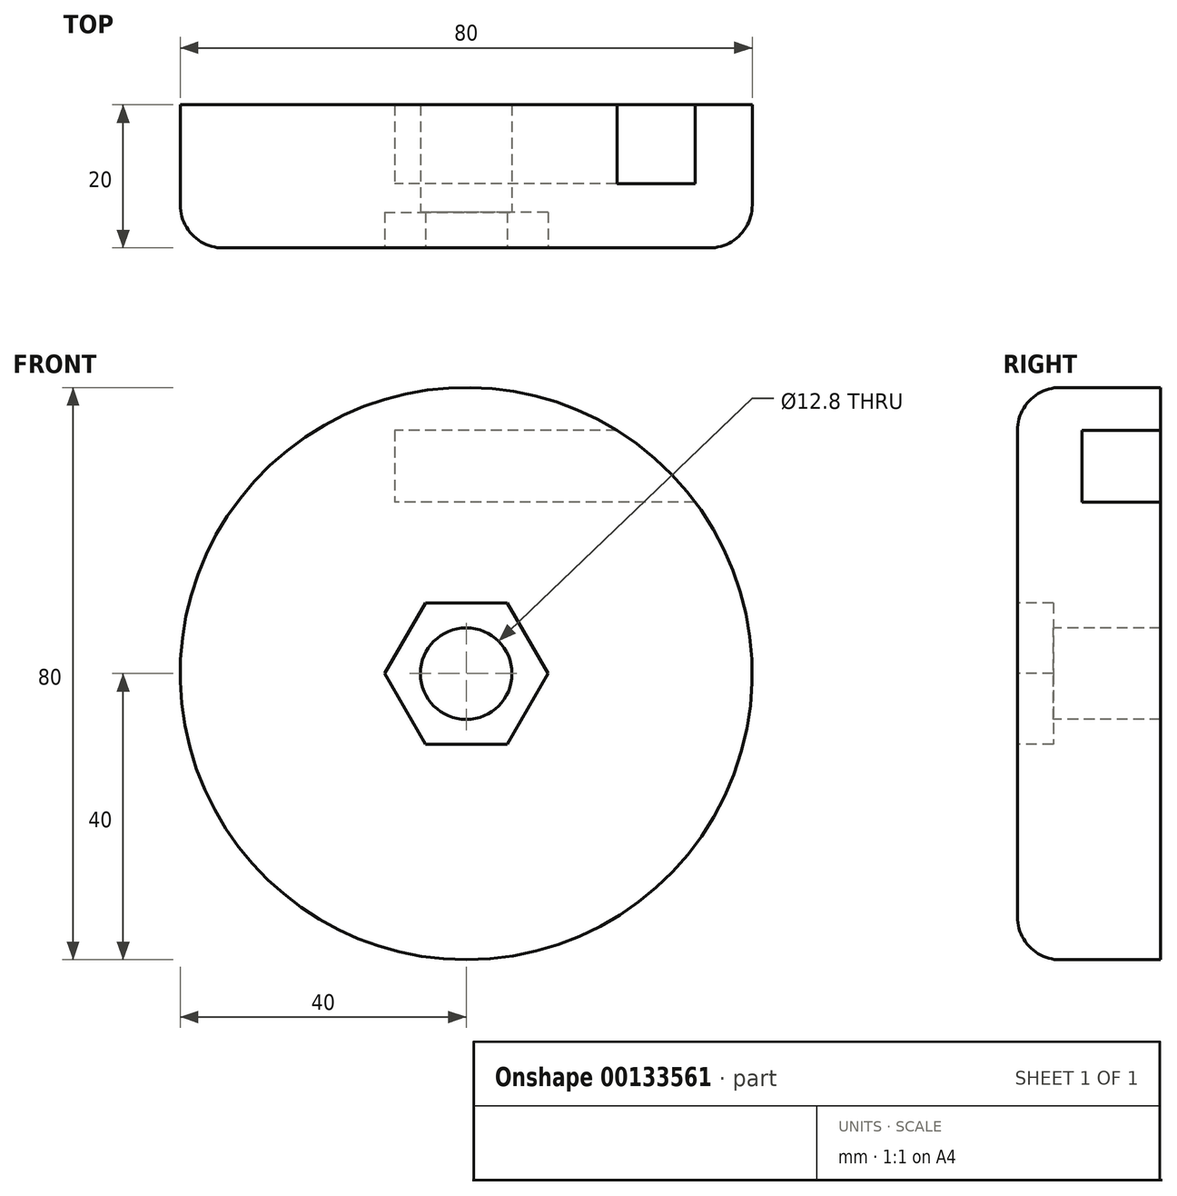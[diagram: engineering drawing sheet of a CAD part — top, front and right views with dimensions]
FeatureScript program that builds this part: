
annotation { "Feature Type Name" : "Feature", "Feature Type Description" : "" }
export const myFeature = defineFeature(function(context is Context, id is Id, definition is map)
    precondition{}
    {
        {
            var Q0;
            Q0=qCreatedBy(makeId("Front.planeOp"),FACE);
            var sketch = newSketch(context, id + "F0", { "sketchPlane" : qUnion([Q0])});
            skCircle(sketch, "E0", {"center": v(0, 0) * mm, "radius": 40 * mm});
            skSolve(sketch);
        }
        {
            var Q0;
            Q0 = qSketchRegion(id + "F0", true);
            extrude(context, id + "F1", {"entities" : qUnion([Q0]), "depth" : 20 * mm});
        }
        {
            var Q0;
            Q0=qCreatedBy(makeId("Right.planeOp"),FACE);
            var sketch = newSketch(context, id + "F2", { "sketchPlane" : qUnion([Q0])});
            skLineSegment(sketch, "E1.bottom", {"start": v(0, 34) * mm, "end": v(-11, 34) * mm});
            skLineSegment(sketch, "E1.top", {"start": v(0, 24) * mm, "end": v(-11, 24) * mm});
            skLineSegment(sketch, "E1.left", {"start": v(0, 34) * mm, "end": v(0, 24) * mm});
            skLineSegment(sketch, "E1.right", {"start": v(-11, 34) * mm, "end": v(-11, 24) * mm});
            skSolve(sketch);
        }
        {
            var Q0;
            Q0 = qSketchRegion(id + "F2", true);
            extrude(context, id + "F3", {"entities" : qUnion([Q0]), "operationType" : NewBodyOperationType.REMOVE, "depth" : 50 * mm, "hasSecondDirection" : true, "secondDirectionOppositeDirection" : true, "secondDirectionDepth" : 10 * mm});
        }
        {
            var Q0;
            Q0=makeQuery(id+"F1.opExtrude","CAP_EDGE",EDGE,{"disambiguationData":[OSD([sQuery(id+"F0.wireOp",EDGE,"E0")])],"isStart":false});
            fillet(context, id + "F4", {"entities" : qUnion([Q0]), "radius" : 6 * mm, "tangentPropagation" : true, "allowEdgeOverflow" : false});
        }
        {
            var Q0;
            Q0=makeQuery(id+"F1.opExtrude","CAP_FACE",FACE,{"disambiguationData":[OSD([sQuery(id+"F0.wireOp",EDGE,"E0")])],"isStart":false});
            var sketch = newSketch(context, id + "F5", { "sketchPlane" : qUnion([Q0])});
            skCircle(sketch, "E2.cCircle", {"center": v(0, 0) * mm, "radius": 9.9 * mm, "construction": true});
            skLineSegment(sketch, "E2.0", {"start": v(5.72, -9.9) * mm, "end": v(-5.72, -9.9) * mm});
            skLineSegment(sketch, "E2.1", {"start": v(-5.72, -9.9) * mm, "end": v(-11.43, 0) * mm});
            skLineSegment(sketch, "E2.2", {"start": v(-11.43, 0) * mm, "end": v(-5.72, 9.9) * mm});
            skLineSegment(sketch, "E2.3", {"start": v(-5.72, 9.9) * mm, "end": v(5.72, 9.9) * mm});
            skLineSegment(sketch, "E2.4", {"start": v(5.72, 9.9) * mm, "end": v(11.43, 0) * mm});
            skLineSegment(sketch, "E2.5", {"start": v(11.43, 0) * mm, "end": v(5.72, -9.9) * mm});
            skPoint(sketch, "E2.0.midPoint", {"position": v(0, -9.9) * mm});
            skSolve(sketch);
        }
        {
            var Q0;
            Q0 = qSketchRegion(id + "F5", true);
            extrude(context, id + "F6", {"entities" : qUnion([Q0]), "operationType" : NewBodyOperationType.REMOVE, "oppositeDirection" : true, "depth" : 5 * mm});
        }
        {
            var Q0;
            Q0=makeQuery(id+"F6.boolean.opBoolean","COPY",FACE,{"derivedFrom":makeQuery(id+"F6.opExtrude","CAP_FACE",FACE,{"disambiguationData":[OSD([sQuery(id+"F5.wireOp",EDGE,"E2.0"),sQuery(id+"F5.wireOp",EDGE,"E2.1"),sQuery(id+"F5.wireOp",EDGE,"E2.2"),sQuery(id+"F5.wireOp",EDGE,"E2.3"),sQuery(id+"F5.wireOp",EDGE,"E2.4"),sQuery(id+"F5.wireOp",EDGE,"E2.5")])],"isStart":false})});
            var sketch = newSketch(context, id + "F7", { "sketchPlane" : qUnion([Q0])});
            skCircle(sketch, "E3", {"center": v(0, 0) * mm, "radius": 6.4 * mm});
            skSolve(sketch);
        }
        {
            var Q0;
            Q0 = qSketchRegion(id + "F7", true);
            extrude(context, id + "F8", {"entities" : qUnion([Q0]), "operationType" : NewBodyOperationType.REMOVE, "oppositeDirection" : true, "depth" : 25 * mm});
        }
    });
